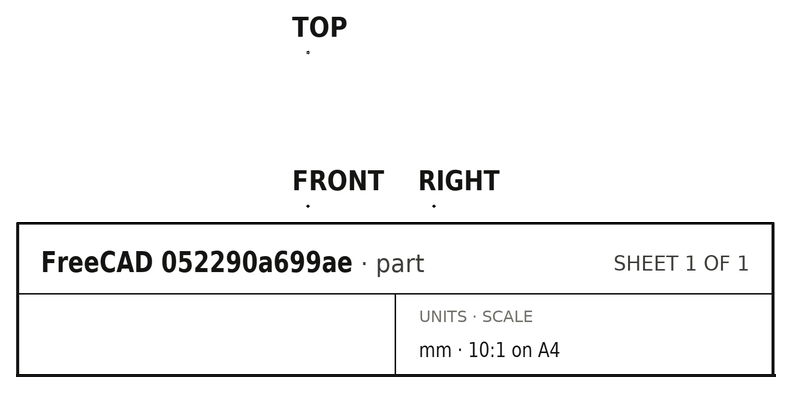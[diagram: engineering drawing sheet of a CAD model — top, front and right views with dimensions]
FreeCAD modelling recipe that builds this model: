
FCSTD DOCUMENT  (FreeCAD 0.19R)
Label: coax
License: All rights reserved
LicenseURL: http://en.wikipedia.org/wiki/All_rights_reserved
objects: Part::Part2DObjectPython×3, Part::Cut×1, App::FeaturePython×1
note: 4 computed .brp shape members not serialized (recipe doc carries the construction recipe); baked Part::Feature solids carry a one-line shape summary decoded from their .brp

FEATURE [Part::Part2DObjectPython] Circle  # Draft 2D object (typed FeaturePython)
  Area = 6.88134e-06
  FirstAngle = 0
  LastAngle = 0
  MakeFace = true
  Radius = 0.00148
FEATURE [Part::Part2DObjectPython] Circle001  # Draft 2D object (typed FeaturePython)
  Area = 5.17848e-07
  FirstAngle = 0
  LastAngle = 0
  MakeFace = true
  Radius = 0.000406
FEATURE [Part::Cut] Cut
  Base = -> Circle
  Tool = -> Circle001
FEATURE [Part::Part2DObjectPython] Line  label="_PV1"  # Draft 2D object (typed FeaturePython)
  Area = 0
  ChamferSize = 0
  Closed = false
  End = (0.00148,0,0)
  FilletRadius = 0
  Length = 0.001074
  MakeFace = true
  Placement = pos=(0.000406,0,0) rot=(0,0,1;0rad)
  Points = (2) [(0,0,0),(0.001074,0,0)]
  Start = (0.000406,0,0)
  Subdivisions = 0
FEATURE [App::FeaturePython] Text  label="_M1(voltage){V1}"  # WARN: FeaturePython — macro-defined, semantics opaque (R4)
  Placement = pos=(0.000624029,-0.00216561,0) rot=(0,0,1;0rad)
  Text = .
